# Revit family: Lighting_Outside_Focus-Lighting_Dua-Low-Bollard
name_source: partatom
category: Lighting Fixtures
revit_build: Autodesk Revit 2018 (Build: 20170223_1515(x64)
units: mm (PartAtom-declared; Revit-internal decimal feet)

## family parameters
Always vertical = Yes
Cut with Voids When Loaded = No
Light Source = Yes
OmniClass Number = 23.80.70.00
OmniClass Title = Lighting
Part Type = Normal
Room Calculation Point = No
Round Connector Dimension = Use Diameter
Shared = No
Work Plane-Based = No

## types (3) — shared parameters
ArticleNumber = 7856-
AssetType = Fixed
BIMObjectName = Lighting_Outside_Focus-Lighting_Dua-Low-Bollard
Brand = Focus lighting
Category = Outside
Collection = Dua
Color = Various
Color Filter = 16777215
Designer = Juul | Frost Arkitekter
Dimming Lamp Color Temperature Shift = <None>
DurationUnit = Hours
ExpectedLife = Operational life min 100,000 hours at ta max 25° C, L80B10.
Features = Mounting For embedment or on flanged base. Connection max three cables 5x16 mm2.LED type Bridgelux V8 and V6. Power consumption 12 W, 350 mA. Colour rendering min 90 Ra. Colour accuracy 3 steps SDCM.
Finish = Finish Graphite grey: YW355F, Akzo Nobel; Silver grey: Y2370I, Akzo Nobel; Corten brown: YX355F, Akzo Nobel; Black: Noir 900 Sablé, SN351F, Akzo Nobel. Shade Acrylic tube with inside spinned grooves.
HasProtectiveEarth = No
IP_Code = IP66
IfcExportAs = IfcLightFixtureType
IfcExportType = NOTDEFINED
InsulationStandardClass = Class II; use code for Class I
LensMaterial = Microprismatic acrylate
Light Source Symbol Size = 610 mm
LightFixtureMountingType = Surface
LightFixturePlacingType = Floor
Manufacturer = Focus lighting
ManufacturerName = Focus Lighting
ManufacturerURL = https://www.focus-lighting.dk
Material = Aluminium
ModelNumber = 7856-
NBSDescription = General purpose luminaires
NBSReference = 90-60-50/405
Name = Dua-Low-Bollard
NominalCurrent = 0 A
NominalDiameter = 187 mm  [stored 0.613517 ft]
NominalFrequencyRange = 50 Hz
NominalHeight = 575 mm
NominalLength = 187 mm  [stored 0.613517 ft]
NominalRadius = 94 mm
NominalVoltage = 230 V
NominalVoltageCalc = 0 V
NominalWidth = 187 mm  [stored 0.613517 ft]
NumberOfPoles = 1
PhaseAngle = 0.00°
Shape = Sculptured
Size = 187x187x575 mm
TotalWattage = 12 W
URL = https://www.focus-lighting.dk
Uniclass2 = Pr_70_70_49
Uniclass2015Description = Free standing luminaires
Uniclass2015Reference = Pr_70_70_48_32
UsageCurrent = 0 A
Version = 1
VersionDate = 11/02/2021
WarrantyDurationUnit = Years
zero-valued in all types: DefaultElevation, ElectricalDeviceNominalPower, MaintenanceFactor, NumberOfSources

## type names (no varying parameters)
- Dua Low Bollard - 12W, 350 mA, 2700 K, 90 Ra
- Dua Low Bollard - 12W, 350 mA, 3000 K, 90 Ra
- Dua Low Bollard - 12W, 350 mA, 4000 K, 90 Ra

note: column(s) folded — value = type name in every type: Model

note: [stored X ft] marks values corroborated as IEEE doubles in the binary element streams (Revit-internal decimal feet)

## geometry (parser evidence)
native form markers: Sweep x4
no freeform markers — native parametric forms only
